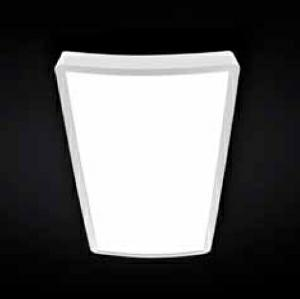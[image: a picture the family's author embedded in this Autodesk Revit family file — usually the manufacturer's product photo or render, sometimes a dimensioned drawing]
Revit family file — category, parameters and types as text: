
# Revit family: spectral_jep_jep-ae-led_3400-840_w
name_source: partatom
category: Lighting Fixtures
revit_build: Autodesk Revit 2016 (Build: 20150220_1215(x64)
units: mm (PartAtom-declared; Revit-internal decimal feet)

## family parameters
Cut with Voids When Loaded = No
Host = Face
Light Source = No
Part Type = Normal
Room Calculation Point = No
Round Connector Dimension = Use Diameter
Shared = No

## types (1)
- SPECTRAL JEP (1 x )
    Apparent Load = 0 VA
    Approval mark = CE
    CIE Flux Codes = 62 88 97 100 100
    Control Gear = Electronic transformer
    Default Elevation = 1800 mm
    Description = SPJ0000007
LED surface-mounted luminaire JEP

Design:
Luminaire housing made of painted plastic with high-efficiency curved mircroprism panel in transparent acrylic. Gear tray in powder coated steel to
accommodate and cool the LED. Steel connection housing ready wired with terminals to accommodate the electronic gear. Bayonet fitting on ceiling
housing for ease of luminaire mounting. Diffuse light distribution. Junction box made of powder coated galvanised steel. Surface-mounted luminaire with
heat-resistant wiring. Protection rating IP20, safety class I.

Colour: Gear tray – similar to RAL 9016 white silk matt
    Height = 35 mm
    Lamp = 1 x
    Lamp count = 1
    Length = 935 mm
    Luminous efficacy = 0 lm/W
    Manufacturer = Ridi
    ModVariant = No
    Model = JEP-AE-LED 3400-840 W
    Mounting Place = Ceiling
    Mounting Type = Surface mounted
    Number of Poles = 1
    OnlyDefault = Yes
    Power Factor = 1
    Product Name = SPECTRAL JEP
    Product group = Ceiling mounted luminaire
    ProductGroupID = 3
    Protection Class = Protection class
    Protection Degree = IP 20
    RlxData = <blob elided: 33037 chars, md5=32645950>
    Socket = socket
    Standby Power = 0 W
    System Light Flux = 0 lm
    System Power = 0 W
    Type Image = jep_deckenaufbau.jpg
    URL = http://reluxnet.relux.com
    VarID = 1
    Voltage = 0 V
    Weight = 0.00 kg
    Width = 360 mm

## geometry (parser evidence)
native form markers: Blend x4, Sweep x10
no freeform markers — native parametric forms only
